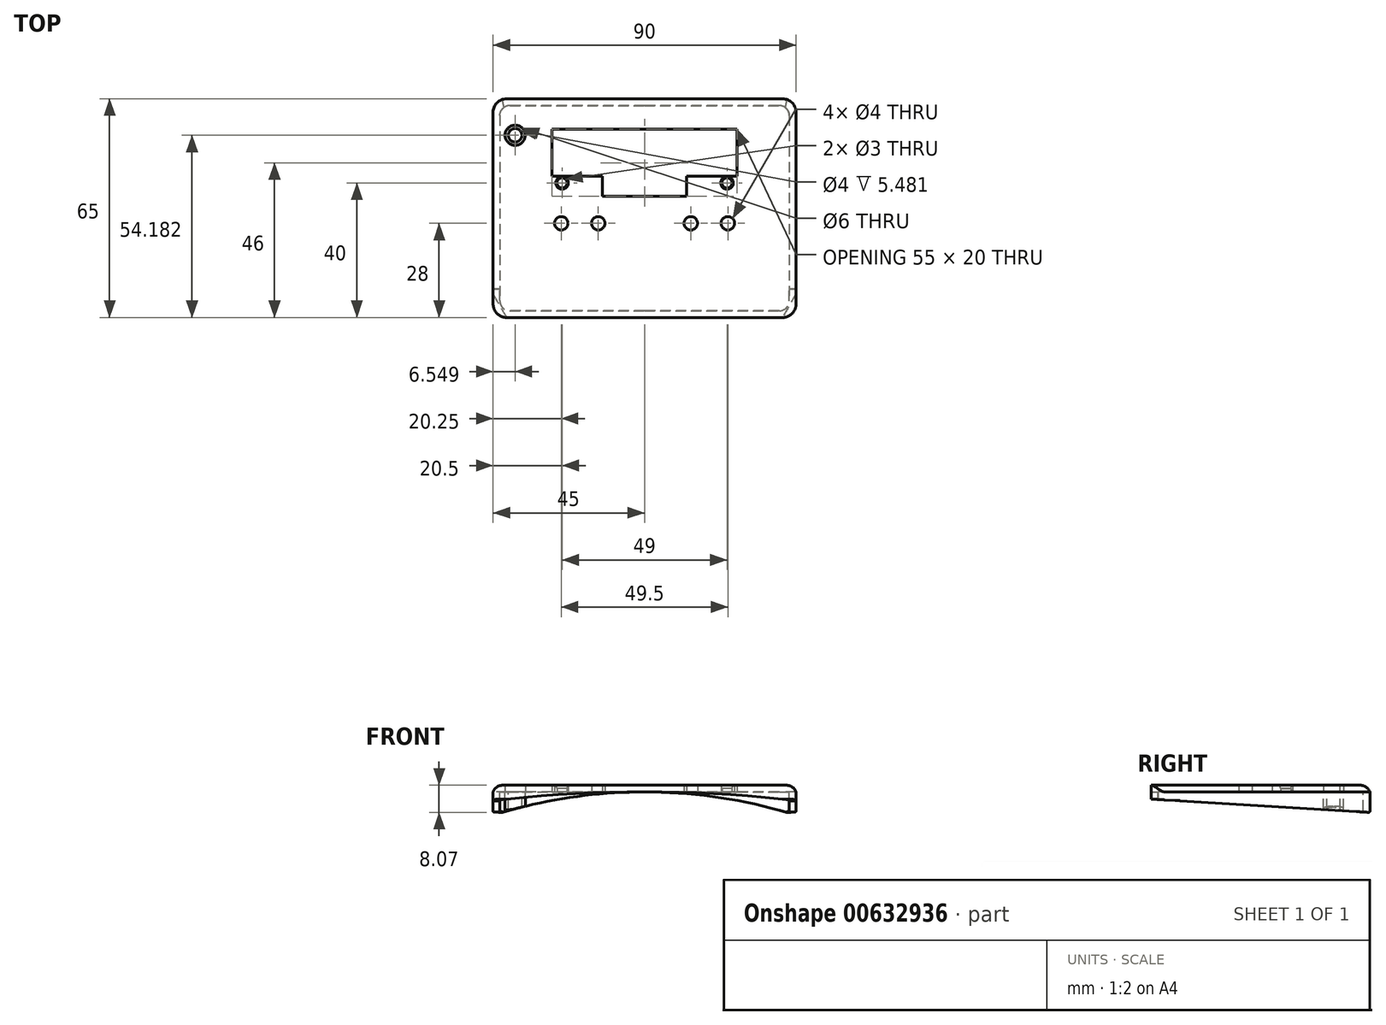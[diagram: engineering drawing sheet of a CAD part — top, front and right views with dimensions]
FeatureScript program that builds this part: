
annotation { "Feature Type Name" : "Feature", "Feature Type Description" : "" }
export const myFeature = defineFeature(function(context is Context, id is Id, definition is map)
    precondition{}
    {
        {
            var Q0;
            Q0=qCreatedBy(makeId("Top.planeOp"),FACE);
            var sketch = newSketch(context, id + "F0", { "sketchPlane" : qUnion([Q0])});
            skLineSegment(sketch, "E0.bottom", {"start": v(-45, 29) * mm, "end": v(45, 29) * mm});
            skLineSegment(sketch, "E0.top", {"start": v(-45, -36) * mm, "end": v(45, -36) * mm});
            skLineSegment(sketch, "E0.left", {"start": v(-45, 29) * mm, "end": v(-45, -36) * mm});
            skLineSegment(sketch, "E0.right", {"start": v(45, 29) * mm, "end": v(45, -36) * mm});
            skLineSegment(sketch, "E1.bottom", {"start": v(-12.5, 20) * mm, "end": v(12.5, 20) * mm});
            skLineSegment(sketch, "E1.top", {"start": v(-12.5, 0) * mm, "end": v(12.5, 0) * mm});
            skLineSegment(sketch, "E1.left", {"start": v(-12.5, 20) * mm, "end": v(-12.5, 0) * mm});
            skLineSegment(sketch, "E1.right", {"start": v(12.5, 20) * mm, "end": v(12.5, 0) * mm});
            skLineSegment(sketch, "E2.bottom", {"start": v(12.5, 20) * mm, "end": v(27.5, 20) * mm});
            skLineSegment(sketch, "E2.top", {"start": v(12.5, 6) * mm, "end": v(27.5, 6) * mm});
            skLineSegment(sketch, "E2.left", {"start": v(12.5, 20) * mm, "end": v(12.5, 6) * mm});
            skLineSegment(sketch, "E2.right", {"start": v(27.5, 20) * mm, "end": v(27.5, 6) * mm});
            skLineSegment(sketch, "E3.bottom", {"start": v(-27.5, 20) * mm, "end": v(-12.5, 20) * mm});
            skLineSegment(sketch, "E3.top", {"start": v(-27.5, 6) * mm, "end": v(-12.5, 6) * mm});
            skLineSegment(sketch, "E3.left", {"start": v(-27.5, 20) * mm, "end": v(-27.5, 6) * mm});
            skLineSegment(sketch, "E3.right", {"start": v(-12.5, 20) * mm, "end": v(-12.5, 6) * mm});
            skCircle(sketch, "E4", {"center": v(-24.75, -8) * mm, "radius": 2 * mm});
            skCircle(sketch, "E5", {"center": v(-13.75, -8) * mm, "radius": 2 * mm});
            skCircle(sketch, "E6", {"center": v(13.75, -8) * mm, "radius": 2 * mm});
            skCircle(sketch, "E7", {"center": v(24.75, -8) * mm, "radius": 2 * mm});
            skPoint(sketch, "E8", {"position": v(0, 0) * mm});
            skCircle(sketch, "E9", {"center": v(-24.5, 4) * mm, "radius": 1.5 * mm});
            skCircle(sketch, "E10", {"center": v(24.5, 4) * mm, "radius": 1.5 * mm});
            skCircle(sketch, "E11", {"center": v(-38.45, 18.18) * mm, "radius": 2 * mm});
            skPoint(sketch, "E12", {"position": v(37, 18) * mm});
            skCircle(sketch, "E13", {"center": v(-38.45, 18.18) * mm, "radius": 3 * mm});
            skSolve(sketch);
        }
        {
            var Q0;
            Q0=makeQuery(id+"F0.imprint","IMPRINT",FACE,{"disambiguationData":[TD([[makeQuery(id+"F0.imprint","IMPRINT",EDGE,{"derivedFrom":sQuery(id+"F0.wireOp",EDGE,"E0.bottom")}),-1.0]])]});
            var Q1;
            Q1=sQuery(id+"F0.wireOp",EDGE,"E0.right");
            var Q2;
            Q2=sQuery(id+"F0.wireOp",EDGE,"E0.top");
            var Q3;
            Q3=sQuery(id+"F0.wireOp",EDGE,"E0.left");
            var Q4;
            Q4=sQuery(id+"F0.wireOp",EDGE,"E0.bottom");
            var Q5;
            Q5=sQuery(id+"F0.wireOp",EDGE,"E7");
            var Q6;
            Q6=sQuery(id+"F0.wireOp",EDGE,"E6");
            var Q7;
            Q7=sQuery(id+"F0.wireOp",EDGE,"E5");
            var Q8;
            Q8=sQuery(id+"F0.wireOp",EDGE,"E4");
            var Q9;
            Q9=sQuery(id+"F0.wireOp",EDGE,"E9");
            var Q10;
            Q10=sQuery(id+"F0.wireOp",EDGE,"E3.top");
            var Q11;
            Q11=sQuery(id+"F0.wireOp",EDGE,"E3.bottom");
            var Q12;
            Q12=sQuery(id+"F0.wireOp",EDGE,"E3.left");
            var Q13;
            Q13=sQuery(id+"F0.wireOp",EDGE,"E1.bottom");
            var Q14;
            Q14=sQuery(id+"F0.wireOp",EDGE,"E1.top");
            var Q15;
            Q15=sQuery(id+"F0.wireOp",EDGE,"E2.top");
            var Q16;
            Q16=sQuery(id+"F0.wireOp",EDGE,"E1.left");
            var Q17;
            Q17=sQuery(id+"F0.wireOp",EDGE,"E1.right");
            var Q18;
            Q18=sQuery(id+"F0.wireOp",EDGE,"E2.bottom");
            var Q19;
            Q19=sQuery(id+"F0.wireOp",EDGE,"E2.right");
            var Q20;
            Q20=sQuery(id+"F0.wireOp",EDGE,"E10");
            extrude(context, id + "F1", {"entities" : qUnion([Q0]), "surfaceEntities" : qUnion([Q1, Q2, Q3, Q4, Q5, Q6, Q7, Q8, Q9, Q10, Q11, Q12, Q13, Q14, Q15, Q16, Q17, Q18, Q19, Q20]), "depth" : 2 * mm, "offsetDistance" : 25 * mm});
        }
        {
            var Q0;
            Q0=makeQuery(id+"F1.opExtrude","SWEPT_EDGE",EDGE,{"disambiguationData":[OSD([sQuery(id+"F0.wireOp",EDGE,"E0.bottom"),sQuery(id+"F0.wireOp",EDGE,"E0.left")])]});
            var Q1;
            Q1=makeQuery(id+"F1.opExtrude","SWEPT_EDGE",EDGE,{"disambiguationData":[OSD([sQuery(id+"F0.wireOp",EDGE,"E0.bottom"),sQuery(id+"F0.wireOp",EDGE,"E0.right")])]});
            var Q2;
            Q2=makeQuery(id+"F1.opExtrude","SWEPT_EDGE",EDGE,{"disambiguationData":[OSD([sQuery(id+"F0.wireOp",EDGE,"E0.top"),sQuery(id+"F0.wireOp",EDGE,"E0.right")])]});
            var Q3;
            Q3=makeQuery(id+"F1.opExtrude","SWEPT_EDGE",EDGE,{"disambiguationData":[OSD([sQuery(id+"F0.wireOp",EDGE,"E0.top"),sQuery(id+"F0.wireOp",EDGE,"E0.left")])]});
            fillet(context, id + "F2", {"entities" : qUnion([Q0, Q1, Q2, Q3]), "radius" : 4 * mm, "tangentPropagation" : true, "allowEdgeOverflow" : false});
        }
        {
            var Q0;
            Q0=makeQuery(id+"F1.opExtrude","CAP_EDGE",EDGE,{"disambiguationData":[OSD([sQuery(id+"F0.wireOp",EDGE,"E0.left")])],"isStart":false});
            var Q1;
            Q1=makeQuery(id+"F1.opExtrude","CAP_EDGE",EDGE,{"disambiguationData":[OSD([sQuery(id+"F0.wireOp",EDGE,"E0.bottom")])],"isStart":false});
            var Q2;
            Q2=makeQuery(id+"F1.opExtrude","CAP_EDGE",EDGE,{"disambiguationData":[OSD([sQuery(id+"F0.wireOp",EDGE,"E0.right")])],"isStart":false});
            fillet(context, id + "F3", {"entities" : qUnion([Q0, Q1, Q2]), "radius" : 3 * mm, "allowEdgeOverflow" : false});
        }
        {
            var Q0;
            Q0=makeQuery(id+"F1.opExtrude","CAP_EDGE",EDGE,{"disambiguationData":[OSD([sQuery(id+"F0.wireOp",EDGE,"E9")])],"isStart":false});
            var Q1;
            Q1=makeQuery(id+"F1.opExtrude","CAP_EDGE",EDGE,{"disambiguationData":[OSD([sQuery(id+"F0.wireOp",EDGE,"E10")])],"isStart":false});
            chamfer(context, id + "F4", {"entities" : qUnion([Q0, Q1]), "chamferType" : ChamferType.OFFSET_ANGLE, "width" : 1 * mm, "oppositeDirection" : false, "angle" : 20 * degree, "tangentPropagation" : true});
        }
        {
            var Q0;
            Q0=makeQuery(id+"F1.opExtrude","CAP_FACE",FACE,{"disambiguationData":[OSD([sQuery(id+"F0.wireOp",EDGE,"E0.bottom"),sQuery(id+"F0.wireOp",EDGE,"E0.top"),sQuery(id+"F0.wireOp",EDGE,"E0.left"),sQuery(id+"F0.wireOp",EDGE,"E0.right"),sQuery(id+"F0.wireOp",EDGE,"E1.bottom"),sQuery(id+"F0.wireOp",EDGE,"E1.top"),sQuery(id+"F0.wireOp",EDGE,"E1.left"),sQuery(id+"F0.wireOp",EDGE,"E1.right"),sQuery(id+"F0.wireOp",EDGE,"E2.bottom"),sQuery(id+"F0.wireOp",EDGE,"E2.top"),sQuery(id+"F0.wireOp",EDGE,"E2.right"),sQuery(id+"F0.wireOp",EDGE,"E3.bottom"),sQuery(id+"F0.wireOp",EDGE,"E3.top"),sQuery(id+"F0.wireOp",EDGE,"E3.left"),sQuery(id+"F0.wireOp",EDGE,"E4"),sQuery(id+"F0.wireOp",EDGE,"E5"),sQuery(id+"F0.wireOp",EDGE,"E6"),sQuery(id+"F0.wireOp",EDGE,"E7"),sQuery(id+"F0.wireOp",EDGE,"E9"),sQuery(id+"F0.wireOp",EDGE,"E10")])],"isStart":true});
            var sketch = newSketch(context, id + "F5", { "sketchPlane" : qUnion([Q0])});
            skLineSegment(sketch, "E14.bottom", {"start": v(45, -29) * mm, "end": v(-45, -29) * mm});
            skLineSegment(sketch, "E14.top", {"start": v(45, 36) * mm, "end": v(-45, 36) * mm});
            skLineSegment(sketch, "E14.left", {"start": v(45, -29) * mm, "end": v(45, 36) * mm});
            skLineSegment(sketch, "E14.right", {"start": v(-45, -29) * mm, "end": v(-45, 36) * mm});
            skLineSegment(sketch, "E15.bottom", {"start": v(40, -27) * mm, "end": v(-40, -27) * mm});
            skLineSegment(sketch, "E15.top", {"start": v(40, 34) * mm, "end": v(-40, 34) * mm});
            skLineSegment(sketch, "E15.left", {"start": v(43, -24) * mm, "end": v(43, 31) * mm});
            skLineSegment(sketch, "E15.right", {"start": v(-43, -24) * mm, "end": v(-43, 31) * mm});
            skPoint(sketch, "E16.visualSharp", {"position": v(43, -27) * mm});
            skArc(sketch, "E16.filletArc", {"start": v(40, -27) * mm, "mid": v(42.12, -26.12) * mm, "end": v(43, -24) * mm});
            skPoint(sketch, "E17.visualSharp", {"position": v(43, 34) * mm});
            skArc(sketch, "E17.filletArc", {"start": v(43, 31) * mm, "mid": v(42.12, 33.12) * mm, "end": v(40, 34) * mm});
            skPoint(sketch, "E18.visualSharp", {"position": v(-43, 34) * mm});
            skArc(sketch, "E18.filletArc", {"start": v(-40, 34) * mm, "mid": v(-42.12, 33.12) * mm, "end": v(-43, 31) * mm});
            skPoint(sketch, "E19.visualSharp", {"position": v(-43, -27) * mm});
            skArc(sketch, "E19.filletArc", {"start": v(-43, -24) * mm, "mid": v(-42.12, -26.12) * mm, "end": v(-40, -27) * mm});
            skCircle(sketch, "E20", {"center": v(-38.45, -18.18) * mm, "radius": 2 * mm});
            skCircle(sketch, "E21", {"center": v(-38.45, -18.18) * mm, "radius": 3 * mm});
            skSolve(sketch);
        }
        {
            var Q0;
            Q0=makeQuery(id+"F5.imprint","IMPRINT",FACE,{"disambiguationData":[TD([[makeQuery(id+"F5.imprint","IMPRINT",EDGE,{"derivedFrom":sQuery(id+"F5.wireOp",EDGE,"E15.bottom")}),1.0]])]});
            var Q1;
            Q1=makeQuery(id+"F5.imprint","IMPRINT",FACE,{"disambiguationData":[TD([[makeQuery(id+"F5.imprint","IMPRINT",EDGE,{"derivedFrom":sQuery(id+"F5.wireOp",EDGE,"E20")}),-1.0]])]});
            extrude(context, id + "F6", {"entities" : qUnion([Q0, Q1]), "operationType" : NewBodyOperationType.ADD, "depth" : 8 * mm, "offsetDistance" : 25 * mm});
        }
        {
            var Q0;
            Q0=qCreatedBy(makeId("Right.planeOp"),FACE);
            var sketch = newSketch(context, id + "F7", { "sketchPlane" : qUnion([Q0])});
            skLineSegment(sketch, "E22.bottom", {"start": v(4, -20) * mm, "end": v(34, -20) * mm});
            skLineSegment(sketch, "E22.top", {"start": v(4, 0) * mm, "end": v(34, 0) * mm});
            skLineSegment(sketch, "E22.left", {"start": v(4, -20) * mm, "end": v(4, 0) * mm});
            skLineSegment(sketch, "E22.right", {"start": v(34, -20) * mm, "end": v(34, 0) * mm});
            skLineSegment(sketch, "E23", {"start": v(34.89, -150) * mm, "end": v(20.3, -150) * mm});
            skSolve(sketch);
        }
        {
            var Q0;
            Q0=makeQuery(id+"F7.imprint","IMPRINT",FACE,{"disambiguationData":[TD([[makeQuery(id+"F7.imprint","IMPRINT",EDGE,{"derivedFrom":sQuery(id+"F7.wireOp",EDGE,"E22.bottom")}),1.0]])]});
            var Q1;
            Q1=sQuery(id+"F7.wireOp",EDGE,"E23");
            revolve(context, id + "F8", {"operationType" : NewBodyOperationType.REMOVE, "surfaceOperationType" : NewSurfaceOperationType.NEW, "entities" : qUnion([Q0]), "axis" : qUnion([Q1]), "revolveType" : RevolveType.FULL, "oppositeDirection" : true});
        }
        {
            var Q0;
            Q0=qCreatedBy(makeId("Right.planeOp"),FACE);
            var sketch = newSketch(context, id + "F9", { "sketchPlane" : qUnion([Q0])});
            skLineSegment(sketch, "E24.bottom", {"start": v(-27.52, -10) * mm, "end": v(-37.52, -10) * mm});
            skLineSegment(sketch, "E24.top", {"start": v(-27.52, 0) * mm, "end": v(-37.52, 0) * mm});
            skLineSegment(sketch, "E24.left", {"start": v(-27.52, -10) * mm, "end": v(-27.52, 0) * mm});
            skLineSegment(sketch, "E24.right", {"start": v(-37.52, -10) * mm, "end": v(-37.52, 0) * mm});
            skLineSegment(sketch, "E25", {"start": v(-41.97, -400) * mm, "end": v(-22.07, -400) * mm});
            skSolve(sketch);
        }
        {
            var Q0;
            Q0 = qSketchRegion(id + "F9", true);
            var Q1;
            Q1=sQuery(id+"F9.wireOp",EDGE,"E25");
            revolve(context, id + "F10", {"operationType" : NewBodyOperationType.REMOVE, "surfaceOperationType" : NewSurfaceOperationType.NEW, "entities" : qUnion([Q0]), "axis" : qUnion([Q1]), "revolveType" : RevolveType.FULL, "oppositeDirection" : true});
        }
        {
            var Q0;
            Q0=qCreatedBy(makeId("Right.planeOp"),FACE);
            var sketch = newSketch(context, id + "F11", { "sketchPlane" : qUnion([Q0])});
            skLineSegment(sketch, "E26", {"start": v(-40.16, -1.85) * mm, "end": v(34.7, -6.43) * mm});
            skLineSegment(sketch, "E27", {"start": v(-40.16, -14.32) * mm, "end": v(34.74, -13.67) * mm});
            skLineSegment(sketch, "E28", {"start": v(-40.16, -1.85) * mm, "end": v(-40.16, -14.32) * mm});
            skLineSegment(sketch, "E29", {"start": v(34.7, -6.43) * mm, "end": v(34.74, -13.67) * mm});
            skSolve(sketch);
        }
        {
            var Q0;
            Q0=makeQuery(id+"F11.imprint","IMPRINT",FACE,{"disambiguationData":[TD([[makeQuery(id+"F11.imprint","IMPRINT",EDGE,{"derivedFrom":sQuery(id+"F11.wireOp",EDGE,"E26")}),-1.0]])]});
            extrude(context, id + "F12", {"entities" : qUnion([Q0]), "operationType" : NewBodyOperationType.REMOVE, "oppositeDirection" : true, "depth" : 100 * mm, "offsetDistance" : 25 * mm, "symmetric" : true});
        }
    });
